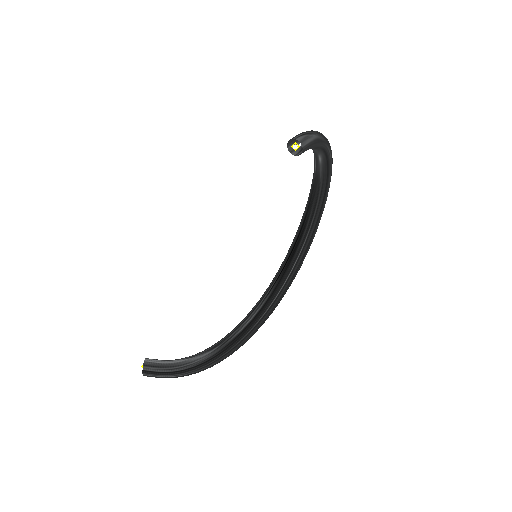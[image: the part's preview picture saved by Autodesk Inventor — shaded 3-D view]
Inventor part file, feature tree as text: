
AUTODESK INVENTOR PART (.ipt)
format: ipt  version: 2022 (Build 260153000, 153)  size: 135,680 bytes
history: native  units: mm (DEFAULTED — no unit token found)
features: other x6, plane x1, sketch x1, sweep x1
ambient origin geometry x8: Origin, YZ Plane, XZ Plane, XY Plane, X Axis, Y Axis, Z Axis, Center Point
bodies: Body1 (feature_tree)
feature tree (9):
  other  "Work Point1"
  other  "Work Point2"
  other  "Wire1"
  plane  "Work Plane1"
  other  "Work Point3"
  other  "Work Point4"
  sketch  "Sketch1"  dims[d0=0.0mm d1=0.0mm]
  other  "Srf1"
  sweep  "SweepSrf1"
